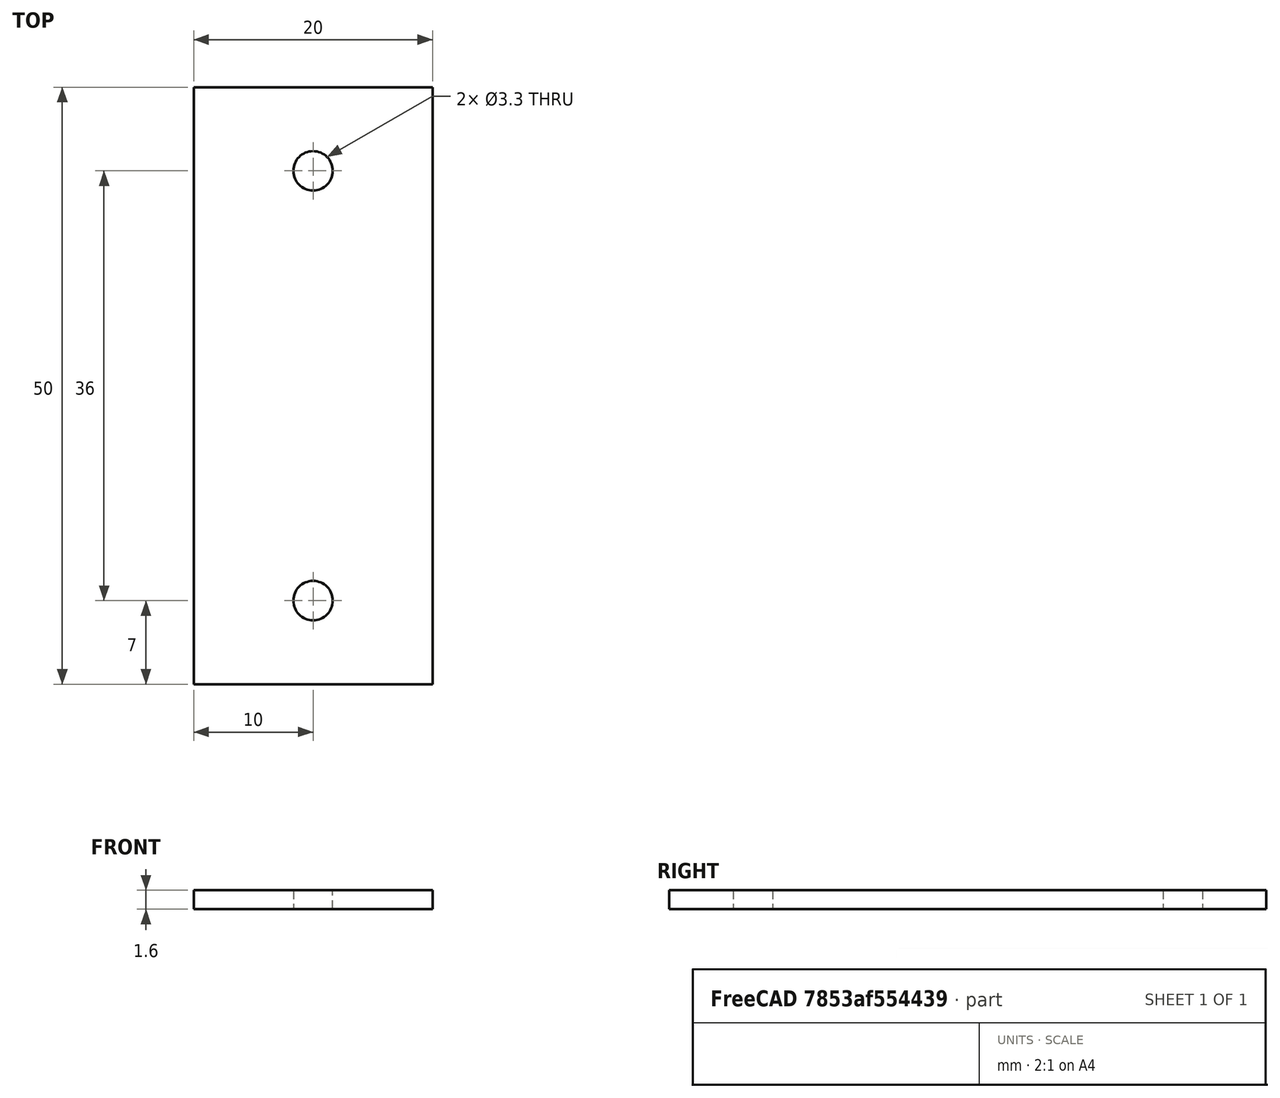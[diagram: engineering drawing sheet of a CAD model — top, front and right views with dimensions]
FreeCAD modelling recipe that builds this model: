
FCSTD DOCUMENT  (FreeCAD 0.16R6706 (Git))
Label: PCB
License: All rights reserved
LicenseURL: http://en.wikipedia.org/wiki/All_rights_reserved
objects: Sketcher::SketchObject×1, PartDesign::Pad×1
note: 3 computed .brp shape members not serialized (recipe doc carries the construction recipe); baked Part::Feature solids carry a one-line shape summary decoded from their .brp

FEATURE [Sketcher::SketchObject] Sketch
  sketch-geometry (6):
    g0: LineSegment StartX=0 StartY=0 StartZ=0 EndX=20 EndY=0 EndZ=0
    g1: LineSegment StartX=20 StartY=0 StartZ=0 EndX=20 EndY=50 EndZ=0
    g2: LineSegment StartX=20 StartY=50 StartZ=0 EndX=0 EndY=50 EndZ=0
    g3: LineSegment StartX=0 StartY=50 StartZ=0 EndX=0 EndY=0 EndZ=0
    g4: Circle CenterX=10 CenterY=43 CenterZ=0 NormalX=0 NormalY=0 NormalZ=1 Radius=1.65
    g5: Circle CenterX=10 CenterY=7 CenterZ=0 NormalX=0 NormalY=0 NormalZ=1 Radius=1.65
  constraints (17):
    c: Coincident(g0,g1)
    c: Coincident(g1,g2)
    c: Coincident(g2,g3)
    c: Coincident(g3,g0)
    c: Horizontal(g0)
    c: Horizontal(g2)
    c: Vertical(g1)
    c: Vertical(g3)
    c: Coincident(g0,g-1)
    c: DistanceY(g-1,g2) = 50
    c: DistanceX(g2,g1) = 20
    c: Radius(g5) = 1.65
    c: Radius(g4) = 1.65
    c: DistanceX(g-1,g5) = 10
    c: DistanceX(g-1,g4) = 10
    c: DistanceY(g-1,g5) = 7
    c: DistanceY(g4,g2) = 7
FEATURE [PartDesign::Pad] Pad
  Length = 1.6
  Length2 = 100
  Sketch = -> Sketch
  Type = 0
